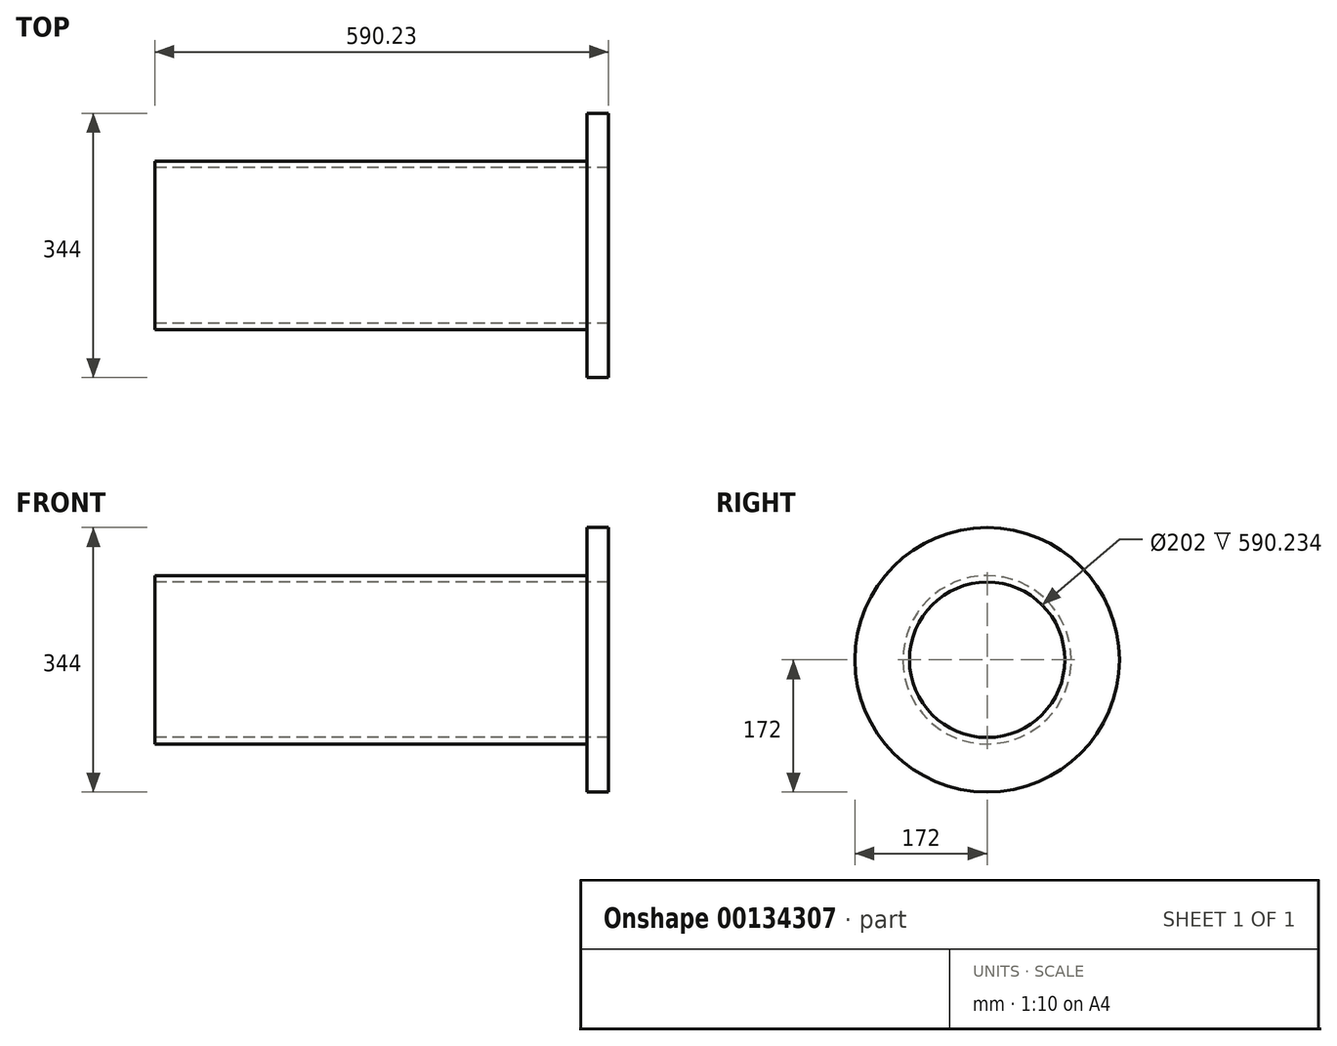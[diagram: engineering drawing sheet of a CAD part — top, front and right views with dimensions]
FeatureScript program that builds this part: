
annotation { "Feature Type Name" : "Feature", "Feature Type Description" : "" }
export const myFeature = defineFeature(function(context is Context, id is Id, definition is map)
    precondition{}
    {
        {
            var Q0;
            Q0=qCreatedBy(makeId("Front.planeOp"),FACE);
            var sketch = newSketch(context, id + "F0", { "sketchPlane" : qUnion([Q0])});
            skLineSegment(sketch, "E0", {"start": v(0, 101) * mm, "end": v(590.23, 101) * mm});
            skLineSegment(sketch, "E1", {"start": v(590.23, 101) * mm, "end": v(590.23, 172) * mm});
            skLineSegment(sketch, "E2", {"start": v(590.23, 172) * mm, "end": v(562.23, 172) * mm});
            skLineSegment(sketch, "E3", {"start": v(562.23, 172) * mm, "end": v(562.23, 109.5) * mm});
            skLineSegment(sketch, "E4", {"start": v(562.23, 109.5) * mm, "end": v(0, 109.5) * mm});
            skLineSegment(sketch, "E5", {"start": v(0, 109.5) * mm, "end": v(0, 101) * mm});
            skLineSegment(sketch, "E6", {"start": v(14.97, 0) * mm, "end": v(222.7, 0) * mm, "construction": true});
            skSolve(sketch);
        }
        {
            var Q0;
            Q0=makeQuery(id+"F0.imprint","IMPRINT",FACE,{"disambiguationData":[TD([[makeQuery(id+"F0.imprint","IMPRINT",EDGE,{"derivedFrom":sQuery(id+"F0.wireOp",EDGE,"E0")}),1.0]])]});
            var Q1;
            Q1=sQuery(id+"F0.wireOp",EDGE,"E6");
            revolve(context, id + "F1", {"entities" : qUnion([Q0]), "axis" : qUnion([Q1]), "revolveType" : RevolveType.FULL});
        }
    });
